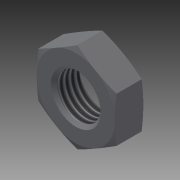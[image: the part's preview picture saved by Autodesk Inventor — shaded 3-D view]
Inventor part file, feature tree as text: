
AUTODESK INVENTOR PART (.ipt)
format: ipt  version: 2014 (Build 180170000, 170)  size: 164,352 bytes
history: native  units: in
note: dims shown in document units (in); Inventor stores cm internally (conversion verified against a paired STEP export)
features: other x70, sketch x3, revolve x2, extrude x1, thread x1
ambient origin geometry x8: Origin, YZ Plane, XZ Plane, XY Plane, X Axis, Y Axis, Z Axis, Center Point
bodies: Solid1 (feature_tree)
feature tree (77):
  sketch  "Sketch_8"  dims[d0=360.0deg d1=0.25in d2=0.0in]
  sketch  "Sketch_10"  dims[d3=360.0deg d4=0.1959in d5=0.0in]
  revolve  "Revolution1"  [1 undecoded]
  extrude  "Extrusion1"  Depth=0.1959in TaperAngle=0.0deg
  revolve  "Revolution2"  [1 undecoded]
  thread  "Thread1"  [1 undecoded]
  other  "NUT_XY"
  other  "NUT_YZ"
  other  "NUT_ZX"
  other  "NUT_X"
  other  "NUT_Y"
  other  "NUT_Z"
  other  "NUT_Center"
  other  "a1_XY"
  other  "a1_YZ"
  other  "a1_ZX"
  other  "a1_X"
  other  "a1_Y"
  other  "a1_Z"
  other  "a1_Center"
  other  "a2_XY"
  other  "a2_YZ"
  other  "a2_ZX"
  other  "a2_X"
  other  "a2_Y"
  other  "a2_Z"
  other  "a2_Center"
  other  "b1_XY"
  other  "b1_YZ"
  other  "b1_ZX"
  other  "b1_X"
  other  "b1_Y"
  other  "b1_Z"
  other  "b1_Center"
  other  "b2_XY"
  other  "b2_YZ"
  other  "b2_ZX"
  other  "b2_X"
  other  "b2_Y"
  other  "b2_Z"
  other  "b2_Center"
  other  "e_XY"
  other  "e_YZ"
  other  "e_ZX"
  other  "e_X"
  other  "e_Y"
  other  "e_Z"
  other  "e_Center"
  other  "ol1_XY"
  other  "ol1_YZ"
  other  "ol1_ZX"
  other  "ol1_X"
  other  "ol1_Y"
  other  "ol1_Z"
  other  "ol1_Center"
  other  "ol2_XY"
  other  "ol2_YZ"
  other  "ol2_ZX"
  other  "ol2_X"
  other  "ol2_Y"
  other  "ol2_Z"
  other  "ol2_Center"
  other  "th1_XY"
  other  "th1_YZ"
  other  "th1_ZX"
  other  "th1_X"
  other  "th1_Y"
  other  "th1_Z"
  other  "th1_Center"
  other  "th2_XY"
  other  "th2_YZ"
  other  "th2_ZX"
  other  "th2_X"
  other  "th2_Y"
  other  "th2_Z"
  other  "th2_Center"
  sketch  "Sketch_11"
note: 3 required parameter values undecoded (feature->parameter linkage not recoverable at this tier; creation-order binding heuristic only, values carry confidence <= 0.55)